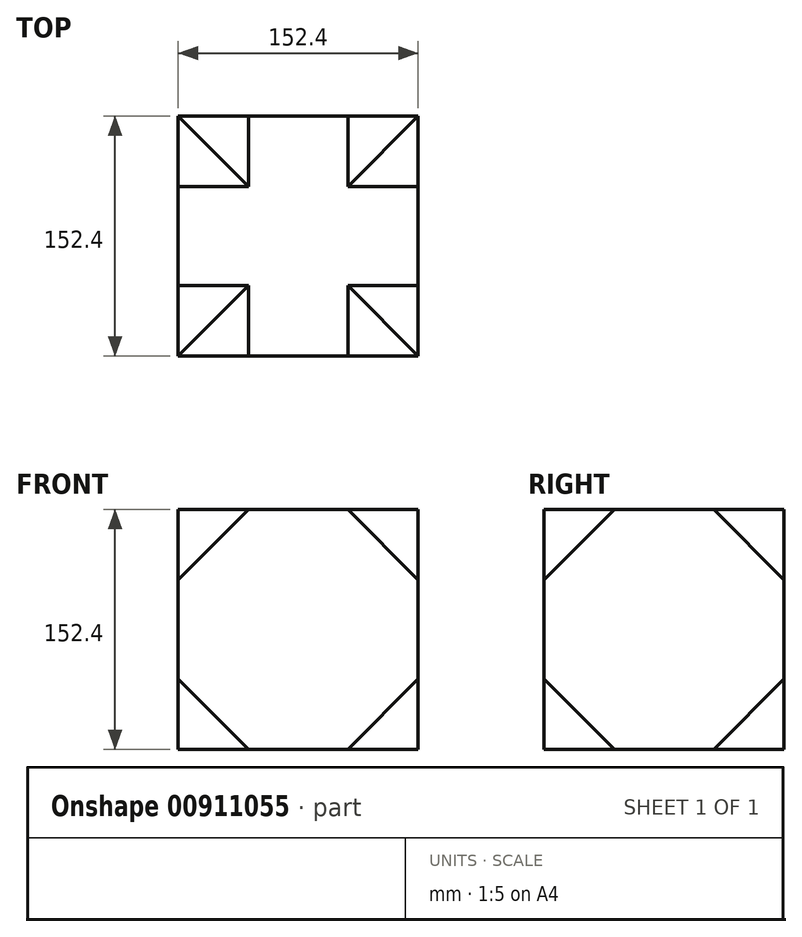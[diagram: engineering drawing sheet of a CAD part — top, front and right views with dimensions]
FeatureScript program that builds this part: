
annotation { "Feature Type Name" : "Feature", "Feature Type Description" : "" }
export const myFeature = defineFeature(function(context is Context, id is Id, definition is map)
    precondition{}
    {
        {
            var Q0;
            Q0=qCreatedBy(makeId("Front.planeOp"),FACE);
            var sketch = newSketch(context, id + "F0", { "sketchPlane" : qUnion([Q0])});
            skCircle(sketch, "E0.cCircle", {"center": v(0, 0) * mm, "radius": 76.2 * mm, "construction": true});
            skLineSegment(sketch, "E0.0", {"start": v(31.56, -76.2) * mm, "end": v(-31.56, -76.2) * mm});
            skLineSegment(sketch, "E0.1", {"start": v(-31.56, -76.2) * mm, "end": v(-76.2, -31.56) * mm});
            skLineSegment(sketch, "E0.2", {"start": v(-76.2, -31.56) * mm, "end": v(-76.2, 31.56) * mm});
            skLineSegment(sketch, "E0.3", {"start": v(-76.2, 31.56) * mm, "end": v(-31.56, 76.2) * mm});
            skLineSegment(sketch, "E0.4", {"start": v(-31.56, 76.2) * mm, "end": v(31.56, 76.2) * mm});
            skLineSegment(sketch, "E0.5", {"start": v(31.56, 76.2) * mm, "end": v(76.2, 31.56) * mm});
            skLineSegment(sketch, "E0.6", {"start": v(76.2, 31.56) * mm, "end": v(76.2, -31.56) * mm});
            skLineSegment(sketch, "E0.7", {"start": v(76.2, -31.56) * mm, "end": v(31.56, -76.2) * mm});
            skPoint(sketch, "E0.0.midPoint", {"position": v(0, -76.2) * mm});
            skSolve(sketch);
        }
        {
            var Q0;
            Q0=makeQuery(id+"F0.imprint","IMPRINT",FACE,{"disambiguationData":[TD([[makeQuery(id+"F0.imprint","IMPRINT",EDGE,{"derivedFrom":sQuery(id+"F0.wireOp",EDGE,"E0.0")}),-1.0]])]});
            extrude(context, id + "F1", {"entities" : qUnion([Q0]), "depth" : 152.4 * mm, "offsetDistance" : 25.4 * mm});
        }
        {
            var Q0;
            Q0=makeQuery(id+"F1.opExtrude","SWEPT_FACE",FACE,{"disambiguationData":[OSD([sQuery(id+"F0.wireOp",EDGE,"E0.2")])]});
            var sketch = newSketch(context, id + "F2", { "sketchPlane" : qUnion([Q0])});
            skLineSegment(sketch, "E1", {"start": v(0, 0) * mm, "end": v(152.4, 0) * mm});
            skLineSegment(sketch, "E2", {"start": v(152.4, 0) * mm, "end": v(76.2, 0) * mm});
            skLineSegment(sketch, "E3", {"start": v(76.2, 0) * mm, "end": v(76.2, -76.2) * mm});
            skCircle(sketch, "E4.cCircle", {"center": v(76.2, 0) * mm, "radius": 76.2 * mm, "construction": true});
            skLineSegment(sketch, "E4.0", {"start": v(107.76, -76.2) * mm, "end": v(44.64, -76.2) * mm});
            skLineSegment(sketch, "E4.1", {"start": v(44.64, -76.2) * mm, "end": v(0, -31.56) * mm});
            skLineSegment(sketch, "E4.2", {"start": v(0, -31.56) * mm, "end": v(0, 31.56) * mm});
            skLineSegment(sketch, "E4.3", {"start": v(0, 31.56) * mm, "end": v(44.64, 76.2) * mm});
            skLineSegment(sketch, "E4.4", {"start": v(44.64, 76.2) * mm, "end": v(107.76, 76.2) * mm});
            skLineSegment(sketch, "E4.5", {"start": v(107.76, 76.2) * mm, "end": v(152.4, 31.56) * mm});
            skLineSegment(sketch, "E4.6", {"start": v(152.4, 31.56) * mm, "end": v(152.4, -31.56) * mm});
            skLineSegment(sketch, "E4.7", {"start": v(152.4, -31.56) * mm, "end": v(107.76, -76.2) * mm});
            skPoint(sketch, "E4.0.midPoint", {"position": v(76.2, -76.2) * mm});
            skSolve(sketch);
        }
        {
            var Q0;
            {var subQ5=sQuery(id+"F2.wireOp",EDGE,"E4.7");Q0=makeQuery(id+"F2.imprint","IMPRINT",FACE,{"disambiguationData":[TD([[makeQuery(id+"F2.imprint","IMPRINT",EDGE,{"derivedFrom":subQ5}),-1.0]])]});}
            var Q1;
            {var subQ5=sQuery(id+"F2.wireOp",EDGE,"E4.1");Q1=makeQuery(id+"F2.imprint","IMPRINT",FACE,{"disambiguationData":[TD([[makeQuery(id+"F2.imprint","IMPRINT",EDGE,{"derivedFrom":subQ5}),-1.0]])]});}
            var Q2;
            {var subQ0=sQuery(id+"F2.wireOp",EDGE,"E1");Q2=makeQuery(id+"F2.imprint","IMPRINT",FACE,{"disambiguationData":[TD([[makeQuery(id+"F2.imprint","IMPRINT",EDGE,{"derivedFrom":subQ0}),-1.0]])]});}
            var Q3;
            {var subQ0=sQuery(id+"F2.wireOp",EDGE,"E2");Q3=makeQuery(id+"F2.imprint","IMPRINT",FACE,{"disambiguationData":[TD([[makeQuery(id+"F2.imprint","IMPRINT",EDGE,{"derivedFrom":subQ0}),1.0]])]});}
            var Q4;
            {var subQ4=sQuery(id+"F2.wireOp",EDGE,"E1");Q4=makeQuery(id+"F2.imprint","IMPRINT",FACE,{"disambiguationData":[TD([[makeQuery(id+"F2.imprint","IMPRINT",EDGE,{"derivedFrom":subQ4}),1.0]])]});}
            var Q5;
            Q5=makeQuery(id+"F2.imprint","IMPRINT",FACE,{"disambiguationData":[TD([[makeQuery(id+"F2.imprint","IMPRINT",EDGE,{"derivedFrom":sQuery(id+"F2.wireOp",EDGE,"E4.3")}),-1.0]])]});
            extrude(context, id + "F3", {"entities" : qUnion([Q0, Q1, Q2, Q3, Q4, Q5]), "operationType" : NewBodyOperationType.ADD, "oppositeDirection" : true, "depth" : 152.4 * mm, "offsetDistance" : 25.4 * mm});
        }
    });
